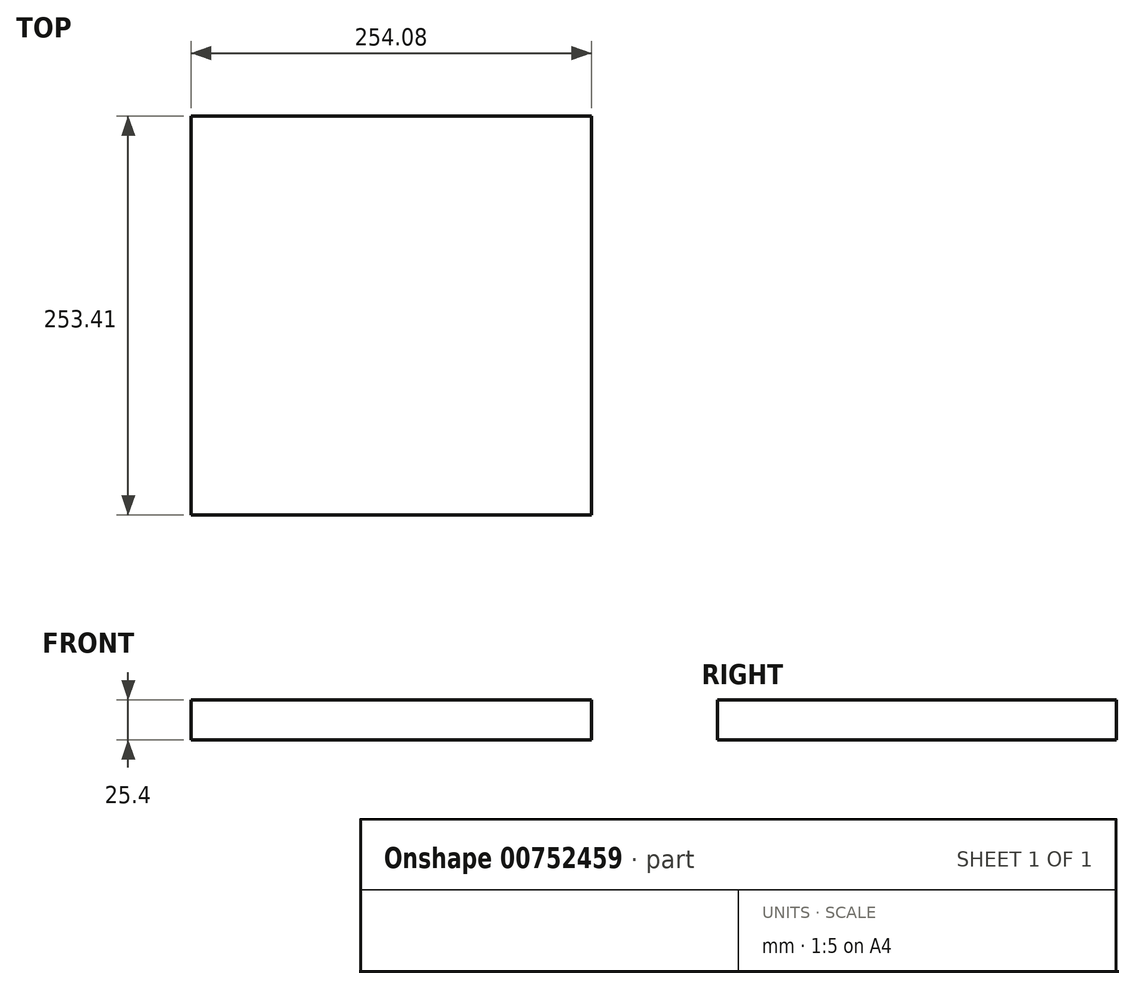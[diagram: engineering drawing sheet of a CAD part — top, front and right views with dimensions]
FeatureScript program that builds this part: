
annotation { "Feature Type Name" : "Feature", "Feature Type Description" : "" }
export const myFeature = defineFeature(function(context is Context, id is Id, definition is map)
    precondition{}
    {
        {
            var Q0;
            Q0=qCreatedBy(makeId("Top.planeOp"),FACE);
            var sketch = newSketch(context, id + "F0", { "sketchPlane" : qUnion([Q0])});
            skLineSegment(sketch, "E0.bottom", {"start": v(-130.17, 0) * mm, "end": v(123.9, 0) * mm});
            skLineSegment(sketch, "E0.top", {"start": v(-130.17, -253.41) * mm, "end": v(123.9, -253.41) * mm});
            skLineSegment(sketch, "E0.left", {"start": v(-130.17, 0) * mm, "end": v(-130.17, -253.41) * mm});
            skLineSegment(sketch, "E0.right", {"start": v(123.9, 0) * mm, "end": v(123.9, -253.41) * mm});
            skSolve(sketch);
        }
        {
            var Q0;
            Q0=makeQuery(id+"F0.imprint","IMPRINT",FACE,{"disambiguationData":[TD([[makeQuery(id+"F0.imprint","IMPRINT",EDGE,{"derivedFrom":sQuery(id+"F0.wireOp",EDGE,"E0.bottom")}),-1.0]])]});
            extrude(context, id + "F1", {"entities" : qUnion([Q0]), "depth" : 25.4 * mm, "offsetDistance" : 25.4 * mm});
        }
    });
